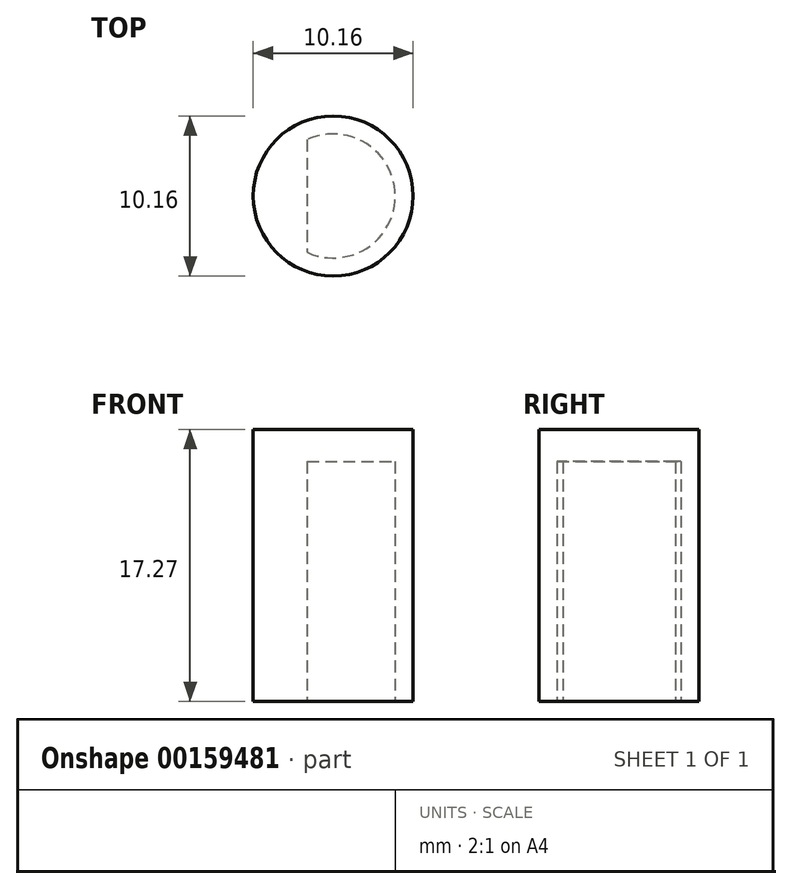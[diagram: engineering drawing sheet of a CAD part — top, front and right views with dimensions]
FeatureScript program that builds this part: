
annotation { "Feature Type Name" : "Feature", "Feature Type Description" : "" }
export const myFeature = defineFeature(function(context is Context, id is Id, definition is map)
    precondition{}
    {
        {
            var Q0;
            Q0=qCreatedBy(makeId("Top.planeOp"),FACE);
            var sketch = newSketch(context, id + "F0", { "sketchPlane" : qUnion([Q0])});
            skCircle(sketch, "E0", {"center": v(0.6, -2.88) * mm, "radius": 5.08 * mm});
            skLineSegment(sketch, "E1", {"start": v(-1.05, -2.88) * mm, "end": v(-1.05, -6.45) * mm});
            skLineSegment(sketch, "E2", {"start": v(-1.05, -2.88) * mm, "end": v(-1.05, 0.7) * mm});
            skArc(sketch, "E3", {"start": v(-1.05, 0.7) * mm, "mid": v(4.54, -2.88) * mm, "end": v(-1.05, -6.45) * mm});
            skSolve(sketch);
        }
        {
            var Q0;
            Q0=makeQuery(id+"F0.imprint","IMPRINT",FACE,{"disambiguationData":[TD([[makeQuery(id+"F0.imprint","IMPRINT",EDGE,{"derivedFrom":sQuery(id+"F0.wireOp",EDGE,"E0")}),1.0]])]});
            extrude(context, id + "F1", {"entities" : qUnion([Q0]), "depth" : 15.24 * mm});
        }
        {
            var Q0;
            Q0=qCreatedBy(makeId("Top.planeOp"),FACE);
            cPlane(context, id + "F2", {"entities" : qUnion([Q0]), "cplaneType" : CPlaneType.OFFSET, "offset" : 15.24 * mm, "width" : 152.4 * mm, "height" : 152.4 * mm});
        }
        {
            var Q0;
            Q0=qCreatedBy(id+"F2.planeOp",FACE);
            var sketch = newSketch(context, id + "F3", { "sketchPlane" : qUnion([Q0])});
            skPoint(sketch, "E4", {"position": v(0.6, -2.88) * mm});
            skCircle(sketch, "E5", {"center": v(0.6, -2.88) * mm, "radius": 5.08 * mm});
            skSolve(sketch);
        }
        {
            var Q0;
            Q0=makeQuery(id+"F3.imprint","IMPRINT",FACE,{"disambiguationData":[TD([[makeQuery(id+"F3.imprint","IMPRINT",EDGE,{"derivedFrom":sQuery(id+"F3.wireOp",EDGE,"E5")}),1.0]])]});
            extrude(context, id + "F4", {"entities" : qUnion([Q0]), "operationType" : NewBodyOperationType.ADD, "depth" : 2.03 * mm});
        }
    });
